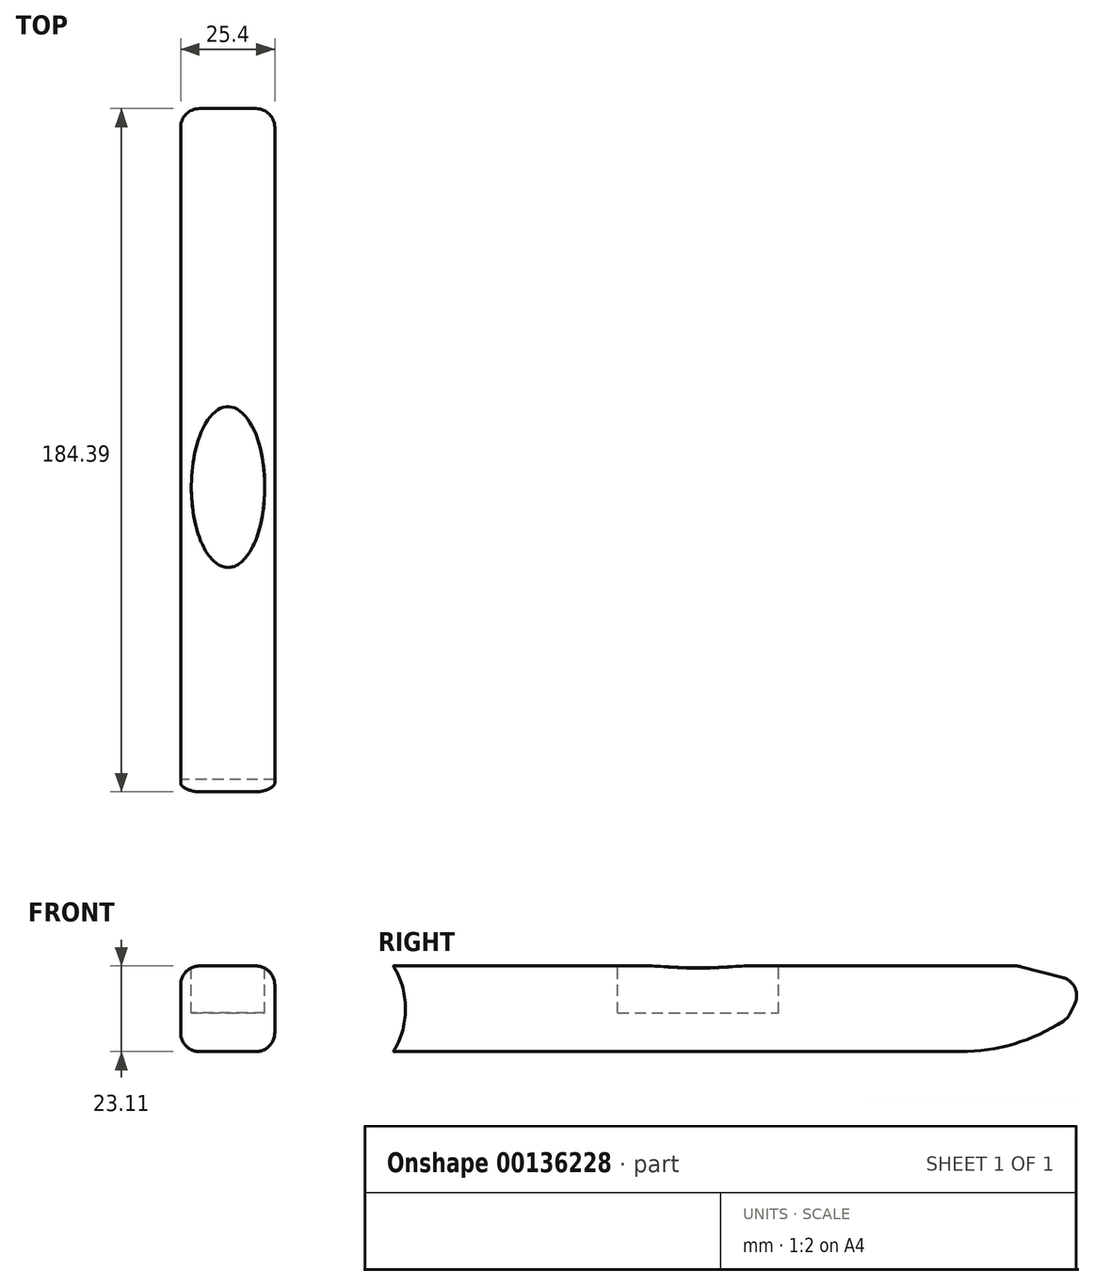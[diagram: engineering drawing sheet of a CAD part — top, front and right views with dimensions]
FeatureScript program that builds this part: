
annotation { "Feature Type Name" : "Feature", "Feature Type Description" : "" }
export const myFeature = defineFeature(function(context is Context, id is Id, definition is map)
    precondition{}
    {
        {
            var Q0;
            Q0=qCreatedBy(makeId("Right.planeOp"),FACE);
            var sketch = newSketch(context, id + "F0", { "sketchPlane" : qUnion([Q0])});
            skLineSegment(sketch, "E0.bottom", {"start": v(-82.26, 28.7) * mm, "end": v(86.38, 28.7) * mm});
            skLineSegment(sketch, "E0.top", {"start": v(-82.26, 5.58) * mm, "end": v(86.38, 5.58) * mm});
            skArc(sketch, "E1", {"start": v(-82.26, 5.58) * mm, "mid": v(-78.97, 17.14) * mm, "end": v(-82.26, 28.7) * mm});
            skLineSegment(sketch, "E2", {"start": v(86.38, 28.7) * mm, "end": v(104.4, 24) * mm});
            skLineSegment(sketch, "E3", {"start": v(104.4, 24) * mm, "end": v(99.7, 14.6) * mm});
            skLineSegment(sketch, "E4", {"start": v(99.7, 14.6) * mm, "end": v(86.38, 5.58) * mm});
            skSolve(sketch);
        }
        {
            var Q0;
            Q0 = qSketchRegion(id + "F0", true);
            extrude(context, id + "F1", {"entities" : qUnion([Q0]), "depth" : 25.4 * mm});
        }
        {
            var Q0;
            Q0=makeQuery(id+"F1.opExtrude","SWEPT_EDGE",EDGE,{"disambiguationData":[OSD([sQuery(id+"F0.wireOp",EDGE,"E0.top"),sQuery(id+"F0.wireOp",EDGE,"E4")])]});
            fillet(context, id + "F2", {"entities" : qUnion([Q0]), "radius" : 50.8 * mm, "tangentPropagation" : true, "allowEdgeOverflow" : false});
        }
        {
            var Q0;
            Q0=makeQuery(id+"F1.opExtrude","SWEPT_EDGE",EDGE,{"disambiguationData":[OSD([sQuery(id+"F0.wireOp",EDGE,"E3"),sQuery(id+"F0.wireOp",EDGE,"E4")])]});
            fillet(context, id + "F3", {"entities" : qUnion([Q0]), "radius" : 5.08 * mm, "tangentPropagation" : true, "allowEdgeOverflow" : false});
        }
        {
            var Q0;
            Q0=makeQuery(id+"F1.opExtrude","SWEPT_EDGE",EDGE,{"disambiguationData":[OSD([sQuery(id+"F0.wireOp",EDGE,"E2"),sQuery(id+"F0.wireOp",EDGE,"E3")])]});
            fillet(context, id + "F4", {"entities" : qUnion([Q0]), "radius" : 5.08 * mm, "tangentPropagation" : true, "allowEdgeOverflow" : false});
        }
        {
            var Q0;
            Q0=makeQuery(id+"F1.opExtrude","SWEPT_EDGE",EDGE,{"disambiguationData":[OSD([sQuery(id+"F0.wireOp",EDGE,"E0.bottom"),sQuery(id+"F0.wireOp",EDGE,"E2")])]});
            fillet(context, id + "F5", {"entities" : qUnion([Q0]), "radius" : 5.08 * mm, "tangentPropagation" : true, "allowEdgeOverflow" : false});
        }
        {
            var Q0;
            Q0=makeQuery(id+"F1.opExtrude","SWEPT_FACE",FACE,{"disambiguationData":[OSD([sQuery(id+"F0.wireOp",EDGE,"E0.bottom")])]});
            var sketch = newSketch(context, id + "F6", { "sketchPlane" : qUnion([Q0])});
            skPoint(sketch, "E5", {"position": v(12.8, 0) * mm});
            skEllipse(sketch, "E6", {"center": v(12.8, 0) * mm, "majorRadius": 21.7 * mm, "minorRadius": 9.9 * mm, "majorAxis": v(0, -1)});
            skSolve(sketch);
        }
        {
            var Q0;
            Q0 = qSketchRegion(id + "F6", true);
            extrude(context, id + "F7", {"entities" : qUnion([Q0]), "operationType" : NewBodyOperationType.REMOVE, "oppositeDirection" : true, "depth" : 12.7 * mm});
        }
        {
            var Q0;
            Q0=makeQuery(id+"F1.opExtrude","CAP_EDGE",EDGE,{"disambiguationData":[OSD([sQuery(id+"F0.wireOp",EDGE,"E0.top")])],"isStart":false});
            var Q1;
            Q1=makeQuery(id+"F1.opExtrude","CAP_EDGE",EDGE,{"disambiguationData":[OSD([sQuery(id+"F0.wireOp",EDGE,"E0.top")])],"isStart":true});
            fillet(context, id + "F8", {"entities" : qUnion([Q0, Q1]), "radius" : 5.08 * mm, "tangentPropagation" : true, "allowEdgeOverflow" : false});
        }
    });
